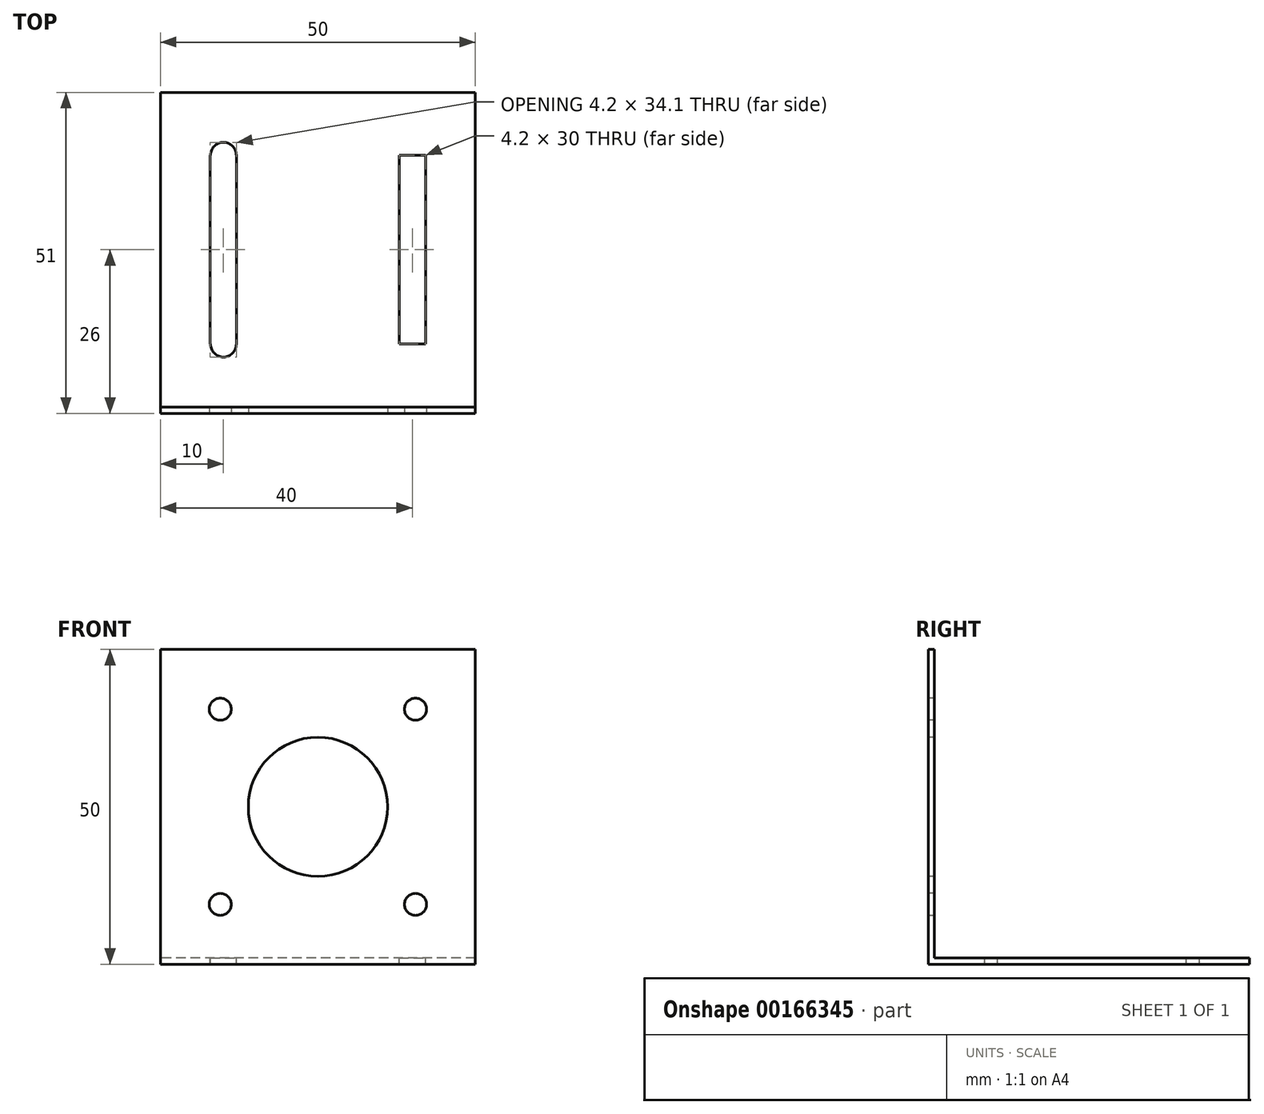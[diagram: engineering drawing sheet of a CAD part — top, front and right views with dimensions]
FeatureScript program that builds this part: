
annotation { "Feature Type Name" : "Feature", "Feature Type Description" : "" }
export const myFeature = defineFeature(function(context is Context, id is Id, definition is map)
    precondition{}
    {
        {
            var Q0;
            Q0=qCreatedBy(makeId("Top.planeOp"),FACE);
            var sketch = newSketch(context, id + "F0", { "sketchPlane" : qUnion([Q0])});
            skLineSegment(sketch, "E0.bottom", {"start": v(25, 25) * mm, "end": v(-25, 25) * mm});
            skLineSegment(sketch, "E0.top", {"start": v(25, -25) * mm, "end": v(-25, -25) * mm});
            skLineSegment(sketch, "E0.left", {"start": v(25, 25) * mm, "end": v(25, -25) * mm});
            skLineSegment(sketch, "E0.right", {"start": v(-25, 25) * mm, "end": v(-25, -25) * mm});
            skPoint(sketch, "E0.middle", {"position": v(0, 0) * mm});
            skSolve(sketch);
        }
        {
            var Q0;
            Q0 = qSketchRegion(id + "F0", true);
            extrude(context, id + "F1", {"entities" : qUnion([Q0]), "depth" : 1 * mm});
        }
        {
            var Q0;
            Q0=makeQuery(id+"F1.opExtrude","SWEPT_FACE",FACE,{"disambiguationData":[OSD([sQuery(id+"F0.wireOp",EDGE,"E0.top")])]});
            var sketch = newSketch(context, id + "F2", { "sketchPlane" : qUnion([Q0])});
            skLineSegment(sketch, "E1.bottom", {"start": v(-25, 0) * mm, "end": v(25, 0) * mm});
            skLineSegment(sketch, "E1.top", {"start": v(-25, 50) * mm, "end": v(25, 50) * mm});
            skLineSegment(sketch, "E1.left", {"start": v(-25, 0) * mm, "end": v(-25, 50) * mm});
            skLineSegment(sketch, "E1.right", {"start": v(25, 0) * mm, "end": v(25, 50) * mm});
            skSolve(sketch);
        }
        {
            var Q0;
            Q0 = qSketchRegion(id + "F2", true);
            extrude(context, id + "F3", {"entities" : qUnion([Q0]), "operationType" : NewBodyOperationType.ADD, "depth" : 1 * mm});
        }
        {
            var Q0;
            Q0=makeQuery(id+"F3.opExtrude","CAP_FACE",FACE,{"disambiguationData":[OSD([sQuery(id+"F2.wireOp",EDGE,"E1.bottom"),sQuery(id+"F2.wireOp",EDGE,"E1.top"),sQuery(id+"F2.wireOp",EDGE,"E1.left"),sQuery(id+"F2.wireOp",EDGE,"E1.right")])],"isStart":false});
            var sketch = newSketch(context, id + "F4", { "sketchPlane" : qUnion([Q0])});
            skLineSegment(sketch, "E2", {"start": v(0, 50) * mm, "end": v(0, 0) * mm});
            skCircle(sketch, "E3", {"center": v(0, 25) * mm, "radius": 11.05 * mm});
            skLineSegment(sketch, "E4.bottom", {"start": v(15.5, 40.5) * mm, "end": v(-15.5, 40.5) * mm});
            skLineSegment(sketch, "E4.top", {"start": v(15.5, 9.5) * mm, "end": v(-15.5, 9.5) * mm});
            skLineSegment(sketch, "E4.left", {"start": v(15.5, 40.5) * mm, "end": v(15.5, 9.5) * mm});
            skLineSegment(sketch, "E4.right", {"start": v(-15.5, 40.5) * mm, "end": v(-15.5, 9.5) * mm});
            skCircle(sketch, "E5", {"center": v(15.5, 40.5) * mm, "radius": 1.75 * mm});
            skCircle(sketch, "E6.1.0", {"center": v(-15.5, 40.5) * mm, "radius": 1.75 * mm});
            skCircle(sketch, "E6.2.0", {"center": v(-15.5, 9.5) * mm, "radius": 1.75 * mm});
            skCircle(sketch, "E6.3.0", {"center": v(15.5, 9.5) * mm, "radius": 1.75 * mm});
            skSolve(sketch);
        }
        {
            var Q0;
            {var subQ0=sQuery(id+"F4.wireOp",EDGE,"E4.left");var subQ1=sQuery(id+"F4.wireOp",EDGE,"E4.bottom");var subQ2=makeQuery(id+"F4.imprint","INTERSECT",VERTEX,{"derivedFrom":[subQ1,subQ0]});Q0=makeQuery(id+"F4.imprint","IMPRINT",FACE,{"disambiguationData":[TD([[makeQuery(id+"F4.imprint","IMPRINT",EDGE,{"disambiguationData":[TD([[subQ2,-1.0]])],"derivedFrom":subQ1}),1.0]])]});}
            var Q1;
            {var subQ0=sQuery(id+"F4.wireOp",EDGE,"E4.left");var subQ1=sQuery(id+"F4.wireOp",EDGE,"E4.bottom");var subQ2=makeQuery(id+"F4.imprint","INTERSECT",VERTEX,{"derivedFrom":[subQ1,subQ0]});Q1=makeQuery(id+"F4.imprint","IMPRINT",FACE,{"disambiguationData":[TD([[makeQuery(id+"F4.imprint","IMPRINT",EDGE,{"disambiguationData":[TD([[subQ2,-1.0]])],"derivedFrom":subQ1}),-1.0]])]});}
            var Q2;
            {var subQ0=sQuery(id+"F4.wireOp",EDGE,"E4.right");var subQ1=sQuery(id+"F4.wireOp",EDGE,"E4.bottom");var subQ2=makeQuery(id+"F4.imprint","INTERSECT",VERTEX,{"derivedFrom":[subQ1,subQ0]});Q2=makeQuery(id+"F4.imprint","IMPRINT",FACE,{"disambiguationData":[TD([[makeQuery(id+"F4.imprint","IMPRINT",EDGE,{"disambiguationData":[TD([[subQ2,1.0]])],"derivedFrom":subQ1}),1.0]])]});}
            var Q3;
            {var subQ0=sQuery(id+"F4.wireOp",EDGE,"E4.right");var subQ1=sQuery(id+"F4.wireOp",EDGE,"E4.bottom");var subQ2=makeQuery(id+"F4.imprint","INTERSECT",VERTEX,{"derivedFrom":[subQ1,subQ0]});Q3=makeQuery(id+"F4.imprint","IMPRINT",FACE,{"disambiguationData":[TD([[makeQuery(id+"F4.imprint","IMPRINT",EDGE,{"disambiguationData":[TD([[subQ2,1.0]])],"derivedFrom":subQ1}),-1.0]])]});}
            var Q4;
            {var subQ0=sQuery(id+"F4.wireOp",EDGE,"E4.left");var subQ1=sQuery(id+"F4.wireOp",EDGE,"E4.top");var subQ2=makeQuery(id+"F4.imprint","INTERSECT",VERTEX,{"derivedFrom":[subQ1,subQ0]});Q4=makeQuery(id+"F4.imprint","IMPRINT",FACE,{"disambiguationData":[TD([[makeQuery(id+"F4.imprint","IMPRINT",EDGE,{"disambiguationData":[TD([[subQ2,-1.0]])],"derivedFrom":subQ1}),-1.0]])]});}
            var Q5;
            {var subQ0=sQuery(id+"F4.wireOp",EDGE,"E4.left");var subQ1=sQuery(id+"F4.wireOp",EDGE,"E4.top");var subQ2=makeQuery(id+"F4.imprint","INTERSECT",VERTEX,{"derivedFrom":[subQ1,subQ0]});Q5=makeQuery(id+"F4.imprint","IMPRINT",FACE,{"disambiguationData":[TD([[makeQuery(id+"F4.imprint","IMPRINT",EDGE,{"disambiguationData":[TD([[subQ2,-1.0]])],"derivedFrom":subQ1}),1.0]])]});}
            var Q6;
            {var subQ0=sQuery(id+"F4.wireOp",EDGE,"E4.right");var subQ1=sQuery(id+"F4.wireOp",EDGE,"E4.top");var subQ2=makeQuery(id+"F4.imprint","INTERSECT",VERTEX,{"derivedFrom":[subQ1,subQ0]});Q6=makeQuery(id+"F4.imprint","IMPRINT",FACE,{"disambiguationData":[TD([[makeQuery(id+"F4.imprint","IMPRINT",EDGE,{"disambiguationData":[TD([[subQ2,1.0]])],"derivedFrom":subQ1}),-1.0]])]});}
            var Q7;
            {var subQ0=sQuery(id+"F4.wireOp",EDGE,"E4.right");var subQ1=sQuery(id+"F4.wireOp",EDGE,"E4.top");var subQ2=makeQuery(id+"F4.imprint","INTERSECT",VERTEX,{"derivedFrom":[subQ1,subQ0]});Q7=makeQuery(id+"F4.imprint","IMPRINT",FACE,{"disambiguationData":[TD([[makeQuery(id+"F4.imprint","IMPRINT",EDGE,{"disambiguationData":[TD([[subQ2,1.0]])],"derivedFrom":subQ1}),1.0]])]});}
            var Q8;
            {var subQ0=sQuery(id+"F4.wireOp",EDGE,"E3");var subQ1=sQuery(id+"F4.wireOp",EDGE,"E2");var subQ2=makeQuery(id+"F4.imprint","INTERSECT",VERTEX,{"disambiguationData":[OD(0.0)],"derivedFrom":[subQ1,subQ0]});Q8=makeQuery(id+"F4.imprint","IMPRINT",FACE,{"disambiguationData":[TD([[makeQuery(id+"F4.imprint","IMPRINT",EDGE,{"disambiguationData":[TD([[subQ2,-1.0]])],"derivedFrom":subQ1}),-1.0]])]});}
            var Q9;
            {var subQ0=sQuery(id+"F4.wireOp",EDGE,"E3");var subQ1=sQuery(id+"F4.wireOp",EDGE,"E2");var subQ2=makeQuery(id+"F4.imprint","INTERSECT",VERTEX,{"disambiguationData":[OD(0.0)],"derivedFrom":[subQ1,subQ0]});Q9=makeQuery(id+"F4.imprint","IMPRINT",FACE,{"disambiguationData":[TD([[makeQuery(id+"F4.imprint","IMPRINT",EDGE,{"disambiguationData":[TD([[subQ2,-1.0]])],"derivedFrom":subQ1}),1.0]])]});}
            extrude(context, id + "F5", {"entities" : qUnion([Q0, Q1, Q2, Q3, Q4, Q5, Q6, Q7, Q8, Q9]), "operationType" : NewBodyOperationType.REMOVE, "oppositeDirection" : true, "depth" : 1 * mm});
        }
        {
            var Q0;
            Q0=makeQuery(id+"F1.opExtrude","CAP_FACE",FACE,{"disambiguationData":[OSD([sQuery(id+"F0.wireOp",EDGE,"E0.bottom"),sQuery(id+"F0.wireOp",EDGE,"E0.top"),sQuery(id+"F0.wireOp",EDGE,"E0.left"),sQuery(id+"F0.wireOp",EDGE,"E0.right")])],"isStart":false});
            var sketch = newSketch(context, id + "F6", { "sketchPlane" : qUnion([Q0])});
            skLineSegment(sketch, "E7.bottom", {"start": v(-15, 15) * mm, "end": v(15, 15) * mm});
            skLineSegment(sketch, "E7.top", {"start": v(-15, -15) * mm, "end": v(15, -15) * mm});
            skLineSegment(sketch, "E7.left", {"start": v(-15, 15) * mm, "end": v(-15, -15) * mm});
            skLineSegment(sketch, "E7.right", {"start": v(15, 15) * mm, "end": v(15, -15) * mm});
            skPoint(sketch, "E7.middle", {"position": v(0, 0) * mm});
            skLineSegment(sketch, "E8.bottom", {"start": v(12.9, 15) * mm, "end": v(17.1, 15) * mm});
            skLineSegment(sketch, "E8.top", {"start": v(12.9, -15) * mm, "end": v(17.1, -15) * mm});
            skLineSegment(sketch, "E8.left", {"start": v(12.9, 15) * mm, "end": v(12.9, -15) * mm});
            skLineSegment(sketch, "E8.right", {"start": v(17.1, 15) * mm, "end": v(17.1, -15) * mm});
            skPoint(sketch, "E8.middle", {"position": v(15, 0) * mm});
            skLineSegment(sketch, "E9.bottom", {"start": v(-17.1, 15) * mm, "end": v(-12.9, 15) * mm});
            skLineSegment(sketch, "E9.top", {"start": v(-17.1, -15) * mm, "end": v(-12.9, -15) * mm});
            skLineSegment(sketch, "E9.left", {"start": v(-17.1, 15) * mm, "end": v(-17.1, -15) * mm});
            skLineSegment(sketch, "E9.right", {"start": v(-12.9, 15) * mm, "end": v(-12.9, -15) * mm});
            skPoint(sketch, "E9.middle", {"position": v(-15, 0) * mm});
            skCircle(sketch, "E10", {"center": v(15, -15) * mm, "radius": 2.05 * mm});
            skCircle(sketch, "E11.1.0", {"center": v(15, 15) * mm, "radius": 2.05 * mm});
            skCircle(sketch, "E11.2.0", {"center": v(-15, 15) * mm, "radius": 2.05 * mm});
            skCircle(sketch, "E11.3.0", {"center": v(-15, -15) * mm, "radius": 2.05 * mm});
            skSolve(sketch);
        }
        {
            var Q0;
            {var subQ0=sQuery(id+"F6.wireOp",EDGE,"E9.bottom");var subQ1=sQuery(id+"F6.wireOp",EDGE,"E7.left");var subQ2=makeQuery(id+"F6.imprint","INTERSECT",VERTEX,{"derivedFrom":[subQ1,subQ0]});Q0=makeQuery(id+"F6.imprint","IMPRINT",FACE,{"disambiguationData":[TD([[makeQuery(id+"F6.imprint","IMPRINT",EDGE,{"disambiguationData":[TD([[subQ2,-1.0]])],"derivedFrom":subQ1}),-1.0]])]});}
            var Q1;
            {var subQ0=sQuery(id+"F6.wireOp",EDGE,"E9.bottom");var subQ1=sQuery(id+"F6.wireOp",EDGE,"E7.left");var subQ2=makeQuery(id+"F6.imprint","INTERSECT",VERTEX,{"derivedFrom":[subQ1,subQ0]});Q1=makeQuery(id+"F6.imprint","IMPRINT",FACE,{"disambiguationData":[TD([[makeQuery(id+"F6.imprint","IMPRINT",EDGE,{"disambiguationData":[TD([[subQ2,-1.0]])],"derivedFrom":subQ1}),1.0]])]});}
            var Q2;
            {var subQ0=sQuery(id+"F6.wireOp",EDGE,"E9.top");var subQ1=sQuery(id+"F6.wireOp",EDGE,"E7.left");var subQ2=makeQuery(id+"F6.imprint","INTERSECT",VERTEX,{"derivedFrom":[subQ1,subQ0]});Q2=makeQuery(id+"F6.imprint","IMPRINT",FACE,{"disambiguationData":[TD([[makeQuery(id+"F6.imprint","IMPRINT",EDGE,{"disambiguationData":[TD([[subQ2,1.0]])],"derivedFrom":subQ1}),-1.0]])]});}
            var Q3;
            {var subQ0=sQuery(id+"F6.wireOp",EDGE,"E9.top");var subQ1=sQuery(id+"F6.wireOp",EDGE,"E7.left");var subQ2=makeQuery(id+"F6.imprint","INTERSECT",VERTEX,{"derivedFrom":[subQ1,subQ0]});Q3=makeQuery(id+"F6.imprint","IMPRINT",FACE,{"disambiguationData":[TD([[makeQuery(id+"F6.imprint","IMPRINT",EDGE,{"disambiguationData":[TD([[subQ2,1.0]])],"derivedFrom":subQ1}),1.0]])]});}
            var Q4;
            {var subQ0=sQuery(id+"F6.wireOp",EDGE,"E8.bottom");var subQ1=sQuery(id+"F6.wireOp",EDGE,"E7.right");var subQ2=makeQuery(id+"F6.imprint","INTERSECT",VERTEX,{"derivedFrom":[subQ1,subQ0]});Q4=makeQuery(id+"F6.imprint","IMPRINT",FACE,{"disambiguationData":[TD([[makeQuery(id+"F6.imprint","IMPRINT",EDGE,{"disambiguationData":[TD([[subQ2,-1.0]])],"derivedFrom":subQ1}),-1.0]])]});}
            var Q5;
            {var subQ0=sQuery(id+"F6.wireOp",EDGE,"E8.bottom");var subQ1=sQuery(id+"F6.wireOp",EDGE,"E7.right");var subQ2=makeQuery(id+"F6.imprint","INTERSECT",VERTEX,{"derivedFrom":[subQ1,subQ0]});Q5=makeQuery(id+"F6.imprint","IMPRINT",FACE,{"disambiguationData":[TD([[makeQuery(id+"F6.imprint","IMPRINT",EDGE,{"disambiguationData":[TD([[subQ2,-1.0]])],"derivedFrom":subQ1}),1.0]])]});}
            var Q6;
            {var subQ0=sQuery(id+"F6.wireOp",EDGE,"E8.top");var subQ1=sQuery(id+"F6.wireOp",EDGE,"E7.right");var subQ2=makeQuery(id+"F6.imprint","INTERSECT",VERTEX,{"derivedFrom":[subQ1,subQ0]});Q6=makeQuery(id+"F6.imprint","IMPRINT",FACE,{"disambiguationData":[TD([[makeQuery(id+"F6.imprint","IMPRINT",EDGE,{"disambiguationData":[TD([[subQ2,1.0]])],"derivedFrom":subQ1}),-1.0]])]});}
            var Q7;
            {var subQ0=sQuery(id+"F6.wireOp",EDGE,"E8.top");var subQ1=sQuery(id+"F6.wireOp",EDGE,"E7.right");var subQ2=makeQuery(id+"F6.imprint","INTERSECT",VERTEX,{"derivedFrom":[subQ1,subQ0]});Q7=makeQuery(id+"F6.imprint","IMPRINT",FACE,{"disambiguationData":[TD([[makeQuery(id+"F6.imprint","IMPRINT",EDGE,{"disambiguationData":[TD([[subQ2,1.0]])],"derivedFrom":subQ1}),1.0]])]});}
            var Q8;
            {var subQ0=sQuery(id+"F6.wireOp",EDGE,"E8.bottom");var subQ1=makeQuery(id+"F6.imprint","INTERSECT",VERTEX,{"derivedFrom":[sQuery(id+"F6.wireOp",EDGE,"E7.right"),subQ0]});Q8=makeQuery(id+"F6.imprint","IMPRINT",FACE,{"disambiguationData":[TD([[makeQuery(id+"F6.imprint","IMPRINT",EDGE,{"disambiguationData":[TD([[subQ1,1.0]])],"derivedFrom":subQ0}),1.0]])]});}
            var Q9;
            {var subQ0=sQuery(id+"F6.wireOp",EDGE,"E8.top");var subQ1=makeQuery(id+"F6.imprint","INTERSECT",VERTEX,{"derivedFrom":[sQuery(id+"F6.wireOp",EDGE,"E7.right"),subQ0]});Q9=makeQuery(id+"F6.imprint","IMPRINT",FACE,{"disambiguationData":[TD([[makeQuery(id+"F6.imprint","IMPRINT",EDGE,{"disambiguationData":[TD([[subQ1,1.0]])],"derivedFrom":subQ0}),-1.0]])]});}
            var Q10;
            {var subQ0=sQuery(id+"F6.wireOp",EDGE,"E9.bottom");var subQ1=makeQuery(id+"F6.imprint","INTERSECT",VERTEX,{"derivedFrom":[sQuery(id+"F6.wireOp",EDGE,"E7.left"),subQ0]});Q10=makeQuery(id+"F6.imprint","IMPRINT",FACE,{"disambiguationData":[TD([[makeQuery(id+"F6.imprint","IMPRINT",EDGE,{"disambiguationData":[TD([[subQ1,1.0]])],"derivedFrom":subQ0}),1.0]])]});}
            var Q11;
            {var subQ0=sQuery(id+"F6.wireOp",EDGE,"E9.top");var subQ1=makeQuery(id+"F6.imprint","INTERSECT",VERTEX,{"derivedFrom":[sQuery(id+"F6.wireOp",EDGE,"E7.left"),subQ0]});Q11=makeQuery(id+"F6.imprint","IMPRINT",FACE,{"disambiguationData":[TD([[makeQuery(id+"F6.imprint","IMPRINT",EDGE,{"disambiguationData":[TD([[subQ1,1.0]])],"derivedFrom":subQ0}),-1.0]])]});}
            var Q12;
            {var subQ0=sQuery(id+"F6.wireOp",EDGE,"E9.left");Q12=makeQuery(id+"F6.imprint","IMPRINT",FACE,{"disambiguationData":[TD([[makeQuery(id+"F6.imprint","IMPRINT",EDGE,{"derivedFrom":subQ0}),1.0]])]});}
            var Q13;
            {var subQ0=sQuery(id+"F6.wireOp",EDGE,"E8.right");Q13=makeQuery(id+"F6.imprint","IMPRINT",FACE,{"disambiguationData":[TD([[makeQuery(id+"F6.imprint","IMPRINT",EDGE,{"derivedFrom":subQ0}),-1.0]])]});}
            var Q14;
            {var subQ0=sQuery(id+"F6.wireOp",EDGE,"E9.right");Q14=makeQuery(id+"F6.imprint","IMPRINT",FACE,{"disambiguationData":[TD([[makeQuery(id+"F6.imprint","IMPRINT",EDGE,{"derivedFrom":subQ0}),-1.0]])]});}
            var Q15;
            {var subQ0=sQuery(id+"F6.wireOp",EDGE,"E8.left");Q15=makeQuery(id+"F6.imprint","IMPRINT",FACE,{"disambiguationData":[TD([[makeQuery(id+"F6.imprint","IMPRINT",EDGE,{"derivedFrom":subQ0}),1.0]])]});}
            extrude(context, id + "F7", {"entities" : qUnion([Q0, Q1, Q2, Q3, Q4, Q5, Q6, Q7, Q8, Q9, Q10, Q11, Q12, Q13, Q14, Q15]), "operationType" : NewBodyOperationType.REMOVE, "oppositeDirection" : true, "depth" : 1 * mm});
        }
    });
